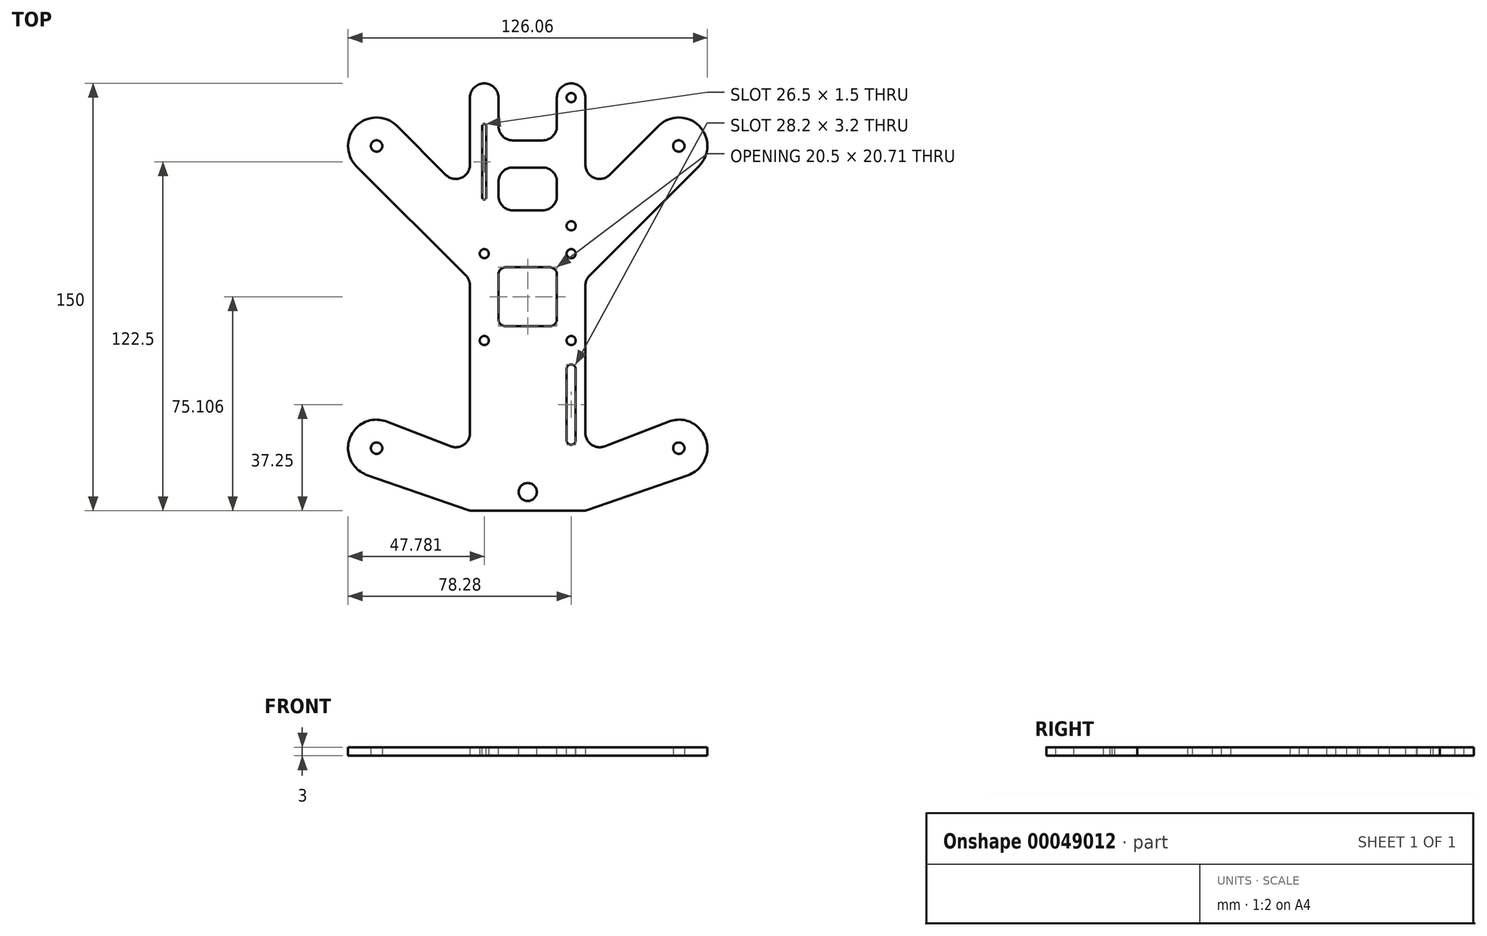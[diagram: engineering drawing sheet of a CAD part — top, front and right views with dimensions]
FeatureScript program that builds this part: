
annotation { "Feature Type Name" : "Feature", "Feature Type Description" : "" }
export const myFeature = defineFeature(function(context is Context, id is Id, definition is map)
    precondition{}
    {
        {
            var Q0;
            Q0=qCreatedBy(makeId("Top.planeOp"),FACE);
            var sketch = newSketch(context, id + "F0", { "sketchPlane" : qUnion([Q0])});
            skCircle(sketch, "E0", {"center": v(0, 0) * mm, "radius": 75 * mm, "construction": true});
            skLineSegment(sketch, "E1", {"start": v(0, 0) * mm, "end": v(53.03, 53.03) * mm, "construction": true});
            skLineSegment(sketch, "E2", {"start": v(0, 0) * mm, "end": v(53.03, -53.03) * mm, "construction": true});
            skCircle(sketch, "E3", {"center": v(53.03, 53.03) * mm, "radius": 10 * mm});
            skCircle(sketch, "E4", {"center": v(53.03, 53.03) * mm, "radius": 2 * mm});
            skLineSegment(sketch, "E5", {"start": v(53.03, 53.03) * mm, "end": v(53.03, 63.03) * mm, "construction": true});
            skLineSegment(sketch, "E6", {"start": v(53.03, 53.03) * mm, "end": v(63.03, 53.03) * mm, "construction": true});
            skLineSegment(sketch, "E7.rect.bottom", {"start": v(-15.25, 15.25) * mm, "end": v(15.25, 15.25) * mm, "construction": true});
            skLineSegment(sketch, "E7.rect.top", {"start": v(-15.25, -15.25) * mm, "end": v(15.25, -15.25) * mm, "construction": true});
            skLineSegment(sketch, "E7.rect.left", {"start": v(-15.25, 15.25) * mm, "end": v(-15.25, -15.25) * mm, "construction": true});
            skLineSegment(sketch, "E7.rect.right", {"start": v(15.25, 15.25) * mm, "end": v(15.25, -15.25) * mm, "construction": true});
            skCircle(sketch, "E8", {"center": v(15.25, 15.25) * mm, "radius": 1.6 * mm});
            skLineSegment(sketch, "E9", {"start": v(0, 0) * mm, "end": v(75, 0) * mm, "construction": true});
            skCircle(sketch, "E10.MirrorC", {"center": v(15.25, -15.25) * mm, "radius": 1.6 * mm});
            skLineSegment(sketch, "E11.bottom", {"start": v(0, 75) * mm, "end": v(15.25, 75) * mm});
            skLineSegment(sketch, "E11.left", {"start": v(0, 75) * mm, "end": v(0, 10.46) * mm});
            skLineSegment(sketch, "E11.right", {"start": v(20.25, 70) * mm, "end": v(20.25, 46.46) * mm});
            skLineSegment(sketch, "E12", {"start": v(53.03, 53.03) * mm, "end": v(53.03, 43.03) * mm, "construction": true});
            skLineSegment(sketch, "E13", {"start": v(53.03, 53.03) * mm, "end": v(43.03, 53.03) * mm, "construction": true});
            skCircle(sketch, "E14.MirrorC", {"center": v(53.03, -53.03) * mm, "radius": 2 * mm});
            skCircle(sketch, "E15.MirrorC", {"center": v(53.03, -53.03) * mm, "radius": 10 * mm});
            skLineSegment(sketch, "E16", {"start": v(45.96, 60.1) * mm, "end": v(28.79, 42.93) * mm});
            skLineSegment(sketch, "E17", {"start": v(60.1, 45.96) * mm, "end": v(21.71, 7.57) * mm});
            skPoint(sketch, "E18.visualSharp", {"position": v(20.25, 34.4) * mm});
            skArc(sketch, "E18.filletArc", {"start": v(20.25, 46.46) * mm, "mid": v(23.34, 41.84) * mm, "end": v(28.79, 42.93) * mm});
            skPoint(sketch, "E19.visualSharp", {"position": v(20.25, 6.1) * mm});
            skArc(sketch, "E19.filletArc", {"start": v(21.71, 7.57) * mm, "mid": v(20.63, 5.95) * mm, "end": v(20.25, 4.04) * mm});
            skPoint(sketch, "E20.visualSharp", {"position": v(20.25, 75) * mm});
            skArc(sketch, "E20.filletArc", {"start": v(20.25, 70) * mm, "mid": v(18.79, 73.54) * mm, "end": v(15.25, 75) * mm});
            skLineSegment(sketch, "E21.bottom", {"start": v(0, 10.46) * mm, "end": v(7.75, 10.46) * mm});
            skLineSegment(sketch, "E21.top", {"start": v(0, -10.25) * mm, "end": v(7.75, -10.25) * mm});
            skLineSegment(sketch, "E21.right", {"start": v(10.25, 7.96) * mm, "end": v(10.25, -7.75) * mm});
            skPoint(sketch, "E22.visualSharp", {"position": v(10.25, -10.25) * mm});
            skArc(sketch, "E22.filletArc", {"start": v(7.75, -10.25) * mm, "mid": v(9.52, -9.52) * mm, "end": v(10.25, -7.75) * mm});
            skPoint(sketch, "E23.visualSharp", {"position": v(10.25, 10.46) * mm});
            skArc(sketch, "E23.filletArc", {"start": v(10.25, 7.96) * mm, "mid": v(9.52, 9.73) * mm, "end": v(7.75, 10.46) * mm});
            skLineSegment(sketch, "E24.trimOffspring", {"start": v(0, -10.25) * mm, "end": v(0, -75) * mm});
            skLineSegment(sketch, "E25", {"start": v(20.25, 4.04) * mm, "end": v(20.25, -47.7) * mm});
            skLineSegment(sketch, "E26", {"start": v(19.4, -75) * mm, "end": v(0, -75) * mm});
            skLineSegment(sketch, "E27", {"start": v(21.05, -74.72) * mm, "end": v(58.39, -61.76) * mm});
            skLineSegment(sketch, "E28", {"start": v(27.05, -52.37) * mm, "end": v(49.42, -43.7) * mm});
            skPoint(sketch, "E29.visualSharp", {"position": v(20.25, -55) * mm});
            skArc(sketch, "E29.filletArc", {"start": v(20.25, -47.7) * mm, "mid": v(22.42, -51.83) * mm, "end": v(27.05, -52.37) * mm});
            skPoint(sketch, "E30.visualSharp", {"position": v(20.25, -75) * mm});
            skArc(sketch, "E30.filletArc", {"start": v(19.4, -75) * mm, "mid": v(20.24, -74.93) * mm, "end": v(21.05, -74.72) * mm});
            skCircle(sketch, "E31", {"center": v(53.03, 53.03) * mm, "radius": 50.8 * mm, "construction": true});
            skCircle(sketch, "E32", {"center": v(53.03, -53.03) * mm, "radius": 38.1 * mm, "construction": true});
            skCircle(sketch, "E33", {"center": v(54.34, 51.82) * mm, "radius": 38.1 * mm, "construction": true});
            skSolve(sketch);
        }
        {
            var Q0;
            Q0 = qSketchRegion(id + "F0", true);
            extrude(context, id + "F1", {"entities" : qUnion([Q0]), "depth" : 3 * mm});
        }
        {
            var Q0;
            Q0=makeQuery(id+"F1.opExtrude","SWEPT_BODY",BODY,{"disambiguationData":[OSD([sQuery(id+"F0.wireOp",EDGE,"E3"),sQuery(id+"F0.wireOp",EDGE,"E4"),sQuery(id+"F0.wireOp",EDGE,"8bb7c5a9-63d8-4c59-b008-a60337fa8d90"),sQuery(id+"F0.wireOp",EDGE,"461b32c1-225a-48ea-9143-580d7a7fa8230.MirrorC"),sQuery(id+"F0.wireOp",EDGE,"e41b9e18-653c-4cae-b2dd-1ab505030cc00.MirrorC"),sQuery(id+"F0.wireOp",EDGE,"770ea447-b549-47c0-91a1-7132aeb66e600.MirrorC"),sQuery(id+"F0.wireOp",EDGE,"E8"),sQuery(id+"F0.wireOp",EDGE,"E10.MirrorC"),sQuery(id+"F0.wireOp",EDGE,"E11.bottom"),sQuery(id+"F0.wireOp",EDGE,"E11.top"),sQuery(id+"F0.wireOp",EDGE,"E11.left"),sQuery(id+"F0.wireOp",EDGE,"E11.right"),sQuery(id+"F0.wireOp",EDGE,"E14.MirrorC"),sQuery(id+"F0.wireOp",EDGE,"07d6f9be-5484-4503-80c9-6294fb1f34722.MirrorC"),sQuery(id+"F0.wireOp",EDGE,"07d6f9be-5484-4503-80c9-6294fb1f34723.MirrorC"),sQuery(id+"F0.wireOp",EDGE,"07d6f9be-5484-4503-80c9-6294fb1f34724.MirrorC"),sQuery(id+"F0.wireOp",EDGE,"07d6f9be-5484-4503-80c9-6294fb1f34725.MirrorC"),sQuery(id+"F0.wireOp",EDGE,"E15.MirrorC"),sQuery(id+"F0.wireOp",EDGE,"E16"),sQuery(id+"F0.wireOp",EDGE,"E17"),sQuery(id+"F0.wireOp",EDGE,"1b5919a4-6bf9-4324-829c-44f6eed34c4f.trimOffspring"),sQuery(id+"F0.wireOp",EDGE,"E18.filletArc"),sQuery(id+"F0.wireOp",EDGE,"E19.filletArc"),sQuery(id+"F0.wireOp",EDGE,"4f1ddc97-92b6-4943-848b-030fe2e09db3"),sQuery(id+"F0.wireOp",EDGE,"c05995a4-ac76-4762-a4bd-68ec24eefa2d"),sQuery(id+"F0.wireOp",EDGE,"34801e48-5682-46ce-81c5-87f2b16cede1.trimOffspring"),sQuery(id+"F0.wireOp",EDGE,"72e0efde-e730-4250-b8e2-a544f2eb8771.filletArc"),sQuery(id+"F0.wireOp",EDGE,"2ddf6d6c-2988-48c9-8456-d2ab87b19bbc.filletArc"),sQuery(id+"F0.wireOp",EDGE,"03b89c73-6ea5-492e-bb8f-ad87dab51ebf.filletArc"),sQuery(id+"F0.wireOp",EDGE,"E20.filletArc")])]});
            var Q1;
            Q1=qCreatedBy(makeId("Right.planeOp"),FACE);
            mirror(context, id + "F2", {"operationType" : NewBodyOperationType.ADD, "entities" : qUnion([Q0]), "mirrorPlane" : qUnion([Q1])});
        }
        {
            var Q0;
            {var subQ0=makeQuery(id+"F1.opExtrude","CAP_FACE",FACE,{"disambiguationData":[OSD([sQuery(id+"F0.wireOp",EDGE,"E3"),sQuery(id+"F0.wireOp",EDGE,"E4"),sQuery(id+"F0.wireOp",EDGE,"E8"),sQuery(id+"F0.wireOp",EDGE,"E10.MirrorC"),sQuery(id+"F0.wireOp",EDGE,"E11.bottom"),sQuery(id+"F0.wireOp",EDGE,"E11.left"),sQuery(id+"F0.wireOp",EDGE,"E11.right"),sQuery(id+"F0.wireOp",EDGE,"E14.MirrorC"),sQuery(id+"F0.wireOp",EDGE,"E15.MirrorC"),sQuery(id+"F0.wireOp",EDGE,"E16"),sQuery(id+"F0.wireOp",EDGE,"E17"),sQuery(id+"F0.wireOp",EDGE,"E18.filletArc"),sQuery(id+"F0.wireOp",EDGE,"E19.filletArc"),sQuery(id+"F0.wireOp",EDGE,"E20.filletArc"),sQuery(id+"F0.wireOp",EDGE,"E21.bottom"),sQuery(id+"F0.wireOp",EDGE,"E21.top"),sQuery(id+"F0.wireOp",EDGE,"E21.right"),sQuery(id+"F0.wireOp",EDGE,"E22.filletArc"),sQuery(id+"F0.wireOp",EDGE,"E23.filletArc"),sQuery(id+"F0.wireOp",EDGE,"E24.trimOffspring"),sQuery(id+"F0.wireOp",EDGE,"E25"),sQuery(id+"F0.wireOp",EDGE,"E26"),sQuery(id+"F0.wireOp",EDGE,"E27"),sQuery(id+"F0.wireOp",EDGE,"E28"),sQuery(id+"F0.wireOp",EDGE,"E29.filletArc"),sQuery(id+"F0.wireOp",EDGE,"E30.filletArc")])],"isStart":false});Q0=makeQuery(id+"F2.boolean.opBoolean","MERGE",FACE,{"derivedFrom":[subQ0,makeQuery(id+"F2.opPattern","COPY",FACE,{"derivedFrom":subQ0,"instanceName":"1"})]});}
            var sketch = newSketch(context, id + "F3", { "sketchPlane" : qUnion([Q0])});
            skCircle(sketch, "E34", {"center": v(15.25, 70) * mm, "radius": 1.6 * mm});
            skCircle(sketch, "E35", {"center": v(15.25, 25) * mm, "radius": 1.6 * mm});
            skSolve(sketch);
        }
        {
            var Q0;
            Q0 = qSketchRegion(id + "F3", true);
            extrude(context, id + "F4", {"entities" : qUnion([Q0]), "operationType" : NewBodyOperationType.REMOVE, "oppositeDirection" : true, "depth" : 25 * mm});
        }
        {
            var Q0;
            {var subQ0=makeQuery(id+"F1.opExtrude","CAP_FACE",FACE,{"disambiguationData":[OSD([sQuery(id+"F0.wireOp",EDGE,"E3"),sQuery(id+"F0.wireOp",EDGE,"E4"),sQuery(id+"F0.wireOp",EDGE,"E8"),sQuery(id+"F0.wireOp",EDGE,"E10.MirrorC"),sQuery(id+"F0.wireOp",EDGE,"E11.bottom"),sQuery(id+"F0.wireOp",EDGE,"E11.left"),sQuery(id+"F0.wireOp",EDGE,"E11.right"),sQuery(id+"F0.wireOp",EDGE,"E14.MirrorC"),sQuery(id+"F0.wireOp",EDGE,"E15.MirrorC"),sQuery(id+"F0.wireOp",EDGE,"E16"),sQuery(id+"F0.wireOp",EDGE,"E17"),sQuery(id+"F0.wireOp",EDGE,"E18.filletArc"),sQuery(id+"F0.wireOp",EDGE,"E19.filletArc"),sQuery(id+"F0.wireOp",EDGE,"E20.filletArc"),sQuery(id+"F0.wireOp",EDGE,"E21.bottom"),sQuery(id+"F0.wireOp",EDGE,"E21.top"),sQuery(id+"F0.wireOp",EDGE,"E21.right"),sQuery(id+"F0.wireOp",EDGE,"E22.filletArc"),sQuery(id+"F0.wireOp",EDGE,"E23.filletArc"),sQuery(id+"F0.wireOp",EDGE,"E24.trimOffspring"),sQuery(id+"F0.wireOp",EDGE,"E25"),sQuery(id+"F0.wireOp",EDGE,"E26"),sQuery(id+"F0.wireOp",EDGE,"E27"),sQuery(id+"F0.wireOp",EDGE,"E28"),sQuery(id+"F0.wireOp",EDGE,"E29.filletArc"),sQuery(id+"F0.wireOp",EDGE,"E30.filletArc")])],"isStart":false});Q0=makeQuery(id+"F2.boolean.opBoolean","MERGE",FACE,{"derivedFrom":[subQ0,makeQuery(id+"F2.opPattern","COPY",FACE,{"derivedFrom":subQ0,"instanceName":"1"})]});}
            var sketch = newSketch(context, id + "F5", { "sketchPlane" : qUnion([Q0])});
            skLineSegment(sketch, "E36", {"start": v(15.25, -15.25) * mm, "end": v(15.25, -25.25) * mm, "construction": true});
            skArc(sketch, "E37", {"start": v(16.85, -25.32) * mm, "mid": v(15.28, -23.65) * mm, "end": v(13.65, -25.25) * mm});
            skArc(sketch, "E38", {"start": v(13.65, -50.25) * mm, "mid": v(15.25, -51.85) * mm, "end": v(16.85, -50.25) * mm});
            skLineSegment(sketch, "E39", {"start": v(13.65, -25.25) * mm, "end": v(13.65, -50.25) * mm});
            skLineSegment(sketch, "E40", {"start": v(16.85, -25.32) * mm, "end": v(16.85, -50.25) * mm});
            skSolve(sketch);
        }
        {
            var Q0;
            Q0 = qSketchRegion(id + "F5", true);
            extrude(context, id + "F6", {"entities" : qUnion([Q0]), "operationType" : NewBodyOperationType.REMOVE, "oppositeDirection" : true, "depth" : 25 * mm});
        }
        {
            var Q0;
            {var subQ0=makeQuery(id+"F1.opExtrude","CAP_FACE",FACE,{"disambiguationData":[OSD([sQuery(id+"F0.wireOp",EDGE,"E3"),sQuery(id+"F0.wireOp",EDGE,"E4"),sQuery(id+"F0.wireOp",EDGE,"E8"),sQuery(id+"F0.wireOp",EDGE,"E10.MirrorC"),sQuery(id+"F0.wireOp",EDGE,"E11.bottom"),sQuery(id+"F0.wireOp",EDGE,"E11.left"),sQuery(id+"F0.wireOp",EDGE,"E11.right"),sQuery(id+"F0.wireOp",EDGE,"E14.MirrorC"),sQuery(id+"F0.wireOp",EDGE,"E15.MirrorC"),sQuery(id+"F0.wireOp",EDGE,"E16"),sQuery(id+"F0.wireOp",EDGE,"E17"),sQuery(id+"F0.wireOp",EDGE,"E18.filletArc"),sQuery(id+"F0.wireOp",EDGE,"E19.filletArc"),sQuery(id+"F0.wireOp",EDGE,"E20.filletArc"),sQuery(id+"F0.wireOp",EDGE,"E21.bottom"),sQuery(id+"F0.wireOp",EDGE,"E21.top"),sQuery(id+"F0.wireOp",EDGE,"E21.right"),sQuery(id+"F0.wireOp",EDGE,"E22.filletArc"),sQuery(id+"F0.wireOp",EDGE,"E23.filletArc"),sQuery(id+"F0.wireOp",EDGE,"E24.trimOffspring"),sQuery(id+"F0.wireOp",EDGE,"E25"),sQuery(id+"F0.wireOp",EDGE,"E26"),sQuery(id+"F0.wireOp",EDGE,"E27"),sQuery(id+"F0.wireOp",EDGE,"E28"),sQuery(id+"F0.wireOp",EDGE,"E29.filletArc"),sQuery(id+"F0.wireOp",EDGE,"E30.filletArc")])],"isStart":false});Q0=makeQuery(id+"F2.boolean.opBoolean","MERGE",FACE,{"derivedFrom":[subQ0,makeQuery(id+"F2.opPattern","COPY",FACE,{"derivedFrom":subQ0,"instanceName":"1"})]});}
            var sketch = newSketch(context, id + "F7", { "sketchPlane" : qUnion([Q0])});
            skCircle(sketch, "E41", {"center": v(0, -68.42) * mm, "radius": 3.18 * mm});
            skPoint(sketch, "E41.centerSnap0", {"position": v(0, -75) * mm});
            skSolve(sketch);
        }
        {
            var Q0;
            Q0 = qSketchRegion(id + "F7", true);
            extrude(context, id + "F8", {"entities" : qUnion([Q0]), "operationType" : NewBodyOperationType.REMOVE, "oppositeDirection" : true, "depth" : 25 * mm});
        }
        {
            var Q0;
            {var subQ0=makeQuery(id+"F1.opExtrude","CAP_FACE",FACE,{"disambiguationData":[OSD([sQuery(id+"F0.wireOp",EDGE,"E3"),sQuery(id+"F0.wireOp",EDGE,"E4"),sQuery(id+"F0.wireOp",EDGE,"E8"),sQuery(id+"F0.wireOp",EDGE,"E10.MirrorC"),sQuery(id+"F0.wireOp",EDGE,"E11.bottom"),sQuery(id+"F0.wireOp",EDGE,"E11.left"),sQuery(id+"F0.wireOp",EDGE,"E11.right"),sQuery(id+"F0.wireOp",EDGE,"E14.MirrorC"),sQuery(id+"F0.wireOp",EDGE,"E15.MirrorC"),sQuery(id+"F0.wireOp",EDGE,"E16"),sQuery(id+"F0.wireOp",EDGE,"E17"),sQuery(id+"F0.wireOp",EDGE,"E18.filletArc"),sQuery(id+"F0.wireOp",EDGE,"E19.filletArc"),sQuery(id+"F0.wireOp",EDGE,"E20.filletArc"),sQuery(id+"F0.wireOp",EDGE,"E21.bottom"),sQuery(id+"F0.wireOp",EDGE,"E21.top"),sQuery(id+"F0.wireOp",EDGE,"E21.right"),sQuery(id+"F0.wireOp",EDGE,"E22.filletArc"),sQuery(id+"F0.wireOp",EDGE,"E23.filletArc"),sQuery(id+"F0.wireOp",EDGE,"E24.trimOffspring"),sQuery(id+"F0.wireOp",EDGE,"E25"),sQuery(id+"F0.wireOp",EDGE,"E26"),sQuery(id+"F0.wireOp",EDGE,"E27"),sQuery(id+"F0.wireOp",EDGE,"E28"),sQuery(id+"F0.wireOp",EDGE,"E29.filletArc"),sQuery(id+"F0.wireOp",EDGE,"E30.filletArc")])],"isStart":false});Q0=makeQuery(id+"F2.boolean.opBoolean","MERGE",FACE,{"derivedFrom":[subQ0,makeQuery(id+"F2.opPattern","COPY",FACE,{"derivedFrom":subQ0,"instanceName":"1"})]});}
            var sketch = newSketch(context, id + "F9", { "sketchPlane" : qUnion([Q0])});
            skLineSegment(sketch, "E42.top", {"start": v(-5.25, 55) * mm, "end": v(5.25, 55) * mm});
            skLineSegment(sketch, "E42.left", {"start": v(-10.25, 70) * mm, "end": v(-10.25, 60) * mm});
            skLineSegment(sketch, "E42.right", {"start": v(10.25, 70) * mm, "end": v(10.25, 60) * mm});
            skLineSegment(sketch, "E43.bottom", {"start": v(-15.25, 75) * mm, "end": v(-15.25, 75) * mm});
            skLineSegment(sketch, "E43.top", {"start": v(-15.25, 79.12) * mm, "end": v(15.25, 79.12) * mm});
            skLineSegment(sketch, "E43.left", {"start": v(-15.25, 75) * mm, "end": v(-15.25, 79.12) * mm});
            skLineSegment(sketch, "E43.right", {"start": v(15.25, 75) * mm, "end": v(15.25, 79.12) * mm});
            skLineSegment(sketch, "E44.trimOffspring", {"start": v(15.25, 75) * mm, "end": v(15.25, 75) * mm});
            skPoint(sketch, "E45.visualSharp", {"position": v(-10.25, 55) * mm});
            skArc(sketch, "E45.filletArc", {"start": v(-10.25, 60) * mm, "mid": v(-8.79, 56.46) * mm, "end": v(-5.25, 55) * mm});
            skPoint(sketch, "E46.visualSharp", {"position": v(10.25, 55) * mm});
            skArc(sketch, "E46.filletArc", {"start": v(5.25, 55) * mm, "mid": v(8.79, 56.46) * mm, "end": v(10.25, 60) * mm});
            skPoint(sketch, "E47.visualSharp", {"position": v(10.25, 75) * mm});
            skArc(sketch, "E47.filletArc", {"start": v(15.25, 75) * mm, "mid": v(11.71, 73.54) * mm, "end": v(10.25, 70) * mm});
            skPoint(sketch, "E48.visualSharp", {"position": v(-10.25, 75) * mm});
            skArc(sketch, "E48.filletArc", {"start": v(-10.25, 70) * mm, "mid": v(-11.71, 73.54) * mm, "end": v(-15.25, 75) * mm});
            skSolve(sketch);
        }
        {
            var Q0;
            Q0 = qSketchRegion(id + "F9", true);
            extrude(context, id + "F10", {"entities" : qUnion([Q0]), "operationType" : NewBodyOperationType.REMOVE, "oppositeDirection" : true, "depth" : 25 * mm});
        }
        {
            var Q0;
            {var subQ0=makeQuery(id+"F1.opExtrude","CAP_FACE",FACE,{"disambiguationData":[OSD([sQuery(id+"F0.wireOp",EDGE,"E3"),sQuery(id+"F0.wireOp",EDGE,"E4"),sQuery(id+"F0.wireOp",EDGE,"E8"),sQuery(id+"F0.wireOp",EDGE,"E10.MirrorC"),sQuery(id+"F0.wireOp",EDGE,"E11.bottom"),sQuery(id+"F0.wireOp",EDGE,"E11.left"),sQuery(id+"F0.wireOp",EDGE,"E11.right"),sQuery(id+"F0.wireOp",EDGE,"E14.MirrorC"),sQuery(id+"F0.wireOp",EDGE,"E15.MirrorC"),sQuery(id+"F0.wireOp",EDGE,"E16"),sQuery(id+"F0.wireOp",EDGE,"E17"),sQuery(id+"F0.wireOp",EDGE,"E18.filletArc"),sQuery(id+"F0.wireOp",EDGE,"E19.filletArc"),sQuery(id+"F0.wireOp",EDGE,"E20.filletArc"),sQuery(id+"F0.wireOp",EDGE,"E21.bottom"),sQuery(id+"F0.wireOp",EDGE,"E21.top"),sQuery(id+"F0.wireOp",EDGE,"E21.right"),sQuery(id+"F0.wireOp",EDGE,"E22.filletArc"),sQuery(id+"F0.wireOp",EDGE,"E23.filletArc"),sQuery(id+"F0.wireOp",EDGE,"E24.trimOffspring"),sQuery(id+"F0.wireOp",EDGE,"E25"),sQuery(id+"F0.wireOp",EDGE,"E26"),sQuery(id+"F0.wireOp",EDGE,"E27"),sQuery(id+"F0.wireOp",EDGE,"E28"),sQuery(id+"F0.wireOp",EDGE,"E29.filletArc"),sQuery(id+"F0.wireOp",EDGE,"E30.filletArc")])],"isStart":false});Q0=makeQuery(id+"F2.boolean.opBoolean","MERGE",FACE,{"derivedFrom":[subQ0,makeQuery(id+"F2.opPattern","COPY",FACE,{"derivedFrom":subQ0,"instanceName":"1"})]});}
            var sketch = newSketch(context, id + "F11", { "sketchPlane" : qUnion([Q0])});
            skLineSegment(sketch, "E49.bottom", {"start": v(5.25, 45.46) * mm, "end": v(-5.25, 45.46) * mm});
            skLineSegment(sketch, "E49.top", {"start": v(5.25, 30.46) * mm, "end": v(-5.25, 30.46) * mm});
            skLineSegment(sketch, "E49.left", {"start": v(10.25, 40.46) * mm, "end": v(10.25, 35.46) * mm});
            skLineSegment(sketch, "E49.right", {"start": v(-10.25, 40.46) * mm, "end": v(-10.25, 35.46) * mm});
            skPoint(sketch, "E49.middle", {"position": v(0, 37.96) * mm});
            skPoint(sketch, "E50.visualSharp", {"position": v(-10.25, 45.46) * mm});
            skArc(sketch, "E50.filletArc", {"start": v(-5.25, 45.46) * mm, "mid": v(-8.79, 44) * mm, "end": v(-10.25, 40.46) * mm});
            skPoint(sketch, "E51.visualSharp", {"position": v(-10.25, 30.46) * mm});
            skArc(sketch, "E51.filletArc", {"start": v(-10.25, 35.46) * mm, "mid": v(-8.79, 31.93) * mm, "end": v(-5.25, 30.46) * mm});
            skPoint(sketch, "E52.visualSharp", {"position": v(10.25, 30.46) * mm});
            skArc(sketch, "E52.filletArc", {"start": v(5.25, 30.46) * mm, "mid": v(8.79, 31.93) * mm, "end": v(10.25, 35.46) * mm});
            skPoint(sketch, "E53.visualSharp", {"position": v(10.25, 45.46) * mm});
            skArc(sketch, "E53.filletArc", {"start": v(10.25, 40.46) * mm, "mid": v(8.79, 44) * mm, "end": v(5.25, 45.46) * mm});
            skSolve(sketch);
        }
        {
            var Q0;
            Q0 = qSketchRegion(id + "F11", true);
            extrude(context, id + "F12", {"entities" : qUnion([Q0]), "operationType" : NewBodyOperationType.REMOVE, "oppositeDirection" : true, "depth" : 25 * mm});
        }
        {
            var Q0;
            {var subQ0=makeQuery(id+"F1.opExtrude","CAP_FACE",FACE,{"disambiguationData":[OSD([sQuery(id+"F0.wireOp",EDGE,"E3"),sQuery(id+"F0.wireOp",EDGE,"E4"),sQuery(id+"F0.wireOp",EDGE,"E8"),sQuery(id+"F0.wireOp",EDGE,"E10.MirrorC"),sQuery(id+"F0.wireOp",EDGE,"E11.bottom"),sQuery(id+"F0.wireOp",EDGE,"E11.left"),sQuery(id+"F0.wireOp",EDGE,"E11.right"),sQuery(id+"F0.wireOp",EDGE,"E14.MirrorC"),sQuery(id+"F0.wireOp",EDGE,"E15.MirrorC"),sQuery(id+"F0.wireOp",EDGE,"E16"),sQuery(id+"F0.wireOp",EDGE,"E17"),sQuery(id+"F0.wireOp",EDGE,"E18.filletArc"),sQuery(id+"F0.wireOp",EDGE,"E19.filletArc"),sQuery(id+"F0.wireOp",EDGE,"E20.filletArc"),sQuery(id+"F0.wireOp",EDGE,"E21.bottom"),sQuery(id+"F0.wireOp",EDGE,"E21.top"),sQuery(id+"F0.wireOp",EDGE,"E21.right"),sQuery(id+"F0.wireOp",EDGE,"E22.filletArc"),sQuery(id+"F0.wireOp",EDGE,"E23.filletArc"),sQuery(id+"F0.wireOp",EDGE,"E24.trimOffspring"),sQuery(id+"F0.wireOp",EDGE,"E25"),sQuery(id+"F0.wireOp",EDGE,"E26"),sQuery(id+"F0.wireOp",EDGE,"E27"),sQuery(id+"F0.wireOp",EDGE,"E28"),sQuery(id+"F0.wireOp",EDGE,"E29.filletArc"),sQuery(id+"F0.wireOp",EDGE,"E30.filletArc")])],"isStart":false});Q0=makeQuery(id+"F2.boolean.opBoolean","MERGE",FACE,{"derivedFrom":[subQ0,makeQuery(id+"F2.opPattern","COPY",FACE,{"derivedFrom":subQ0,"instanceName":"1"})]});}
            var sketch = newSketch(context, id + "F13", { "sketchPlane" : qUnion([Q0])});
            skLineSegment(sketch, "E54", {"start": v(-15.25, 70) * mm, "end": v(-15.25, 25) * mm, "construction": true});
            skArc(sketch, "E55", {"start": v(-14.5, 60) * mm, "mid": v(-15.28, 60.75) * mm, "end": v(-16, 59.94) * mm});
            skArc(sketch, "E56", {"start": v(-16, 35.06) * mm, "mid": v(-15.28, 34.25) * mm, "end": v(-14.5, 35) * mm});
            skLineSegment(sketch, "E57", {"start": v(-14.5, 60) * mm, "end": v(-14.5, 35) * mm});
            skLineSegment(sketch, "E58", {"start": v(-16, 60.06) * mm, "end": v(-16, 34.94) * mm});
            skLineSegment(sketch, "E59", {"start": v(-15.25, 35) * mm, "end": v(-21.44, 35) * mm, "construction": true});
            skLineSegment(sketch, "E60", {"start": v(-21.44, 35) * mm, "end": v(-21.44, 25) * mm, "construction": true});
            skLineSegment(sketch, "E61", {"start": v(-21.44, 25) * mm, "end": v(-15.25, 25) * mm, "construction": true});
            skLineSegment(sketch, "E62", {"start": v(-15.25, 70) * mm, "end": v(-21.44, 70) * mm, "construction": true});
            skLineSegment(sketch, "E63", {"start": v(-21.44, 70) * mm, "end": v(-21.44, 60) * mm, "construction": true});
            skLineSegment(sketch, "E64", {"start": v(-21.44, 60) * mm, "end": v(-15.25, 60) * mm, "construction": true});
            skSolve(sketch);
        }
        {
            var Q0;
            Q0 = qSketchRegion(id + "F13", true);
            extrude(context, id + "F14", {"entities" : qUnion([Q0]), "operationType" : NewBodyOperationType.REMOVE, "endBound" : BoundingType.THROUGH_ALL, "oppositeDirection" : true, "depth" : 25 * mm});
        }
    });
